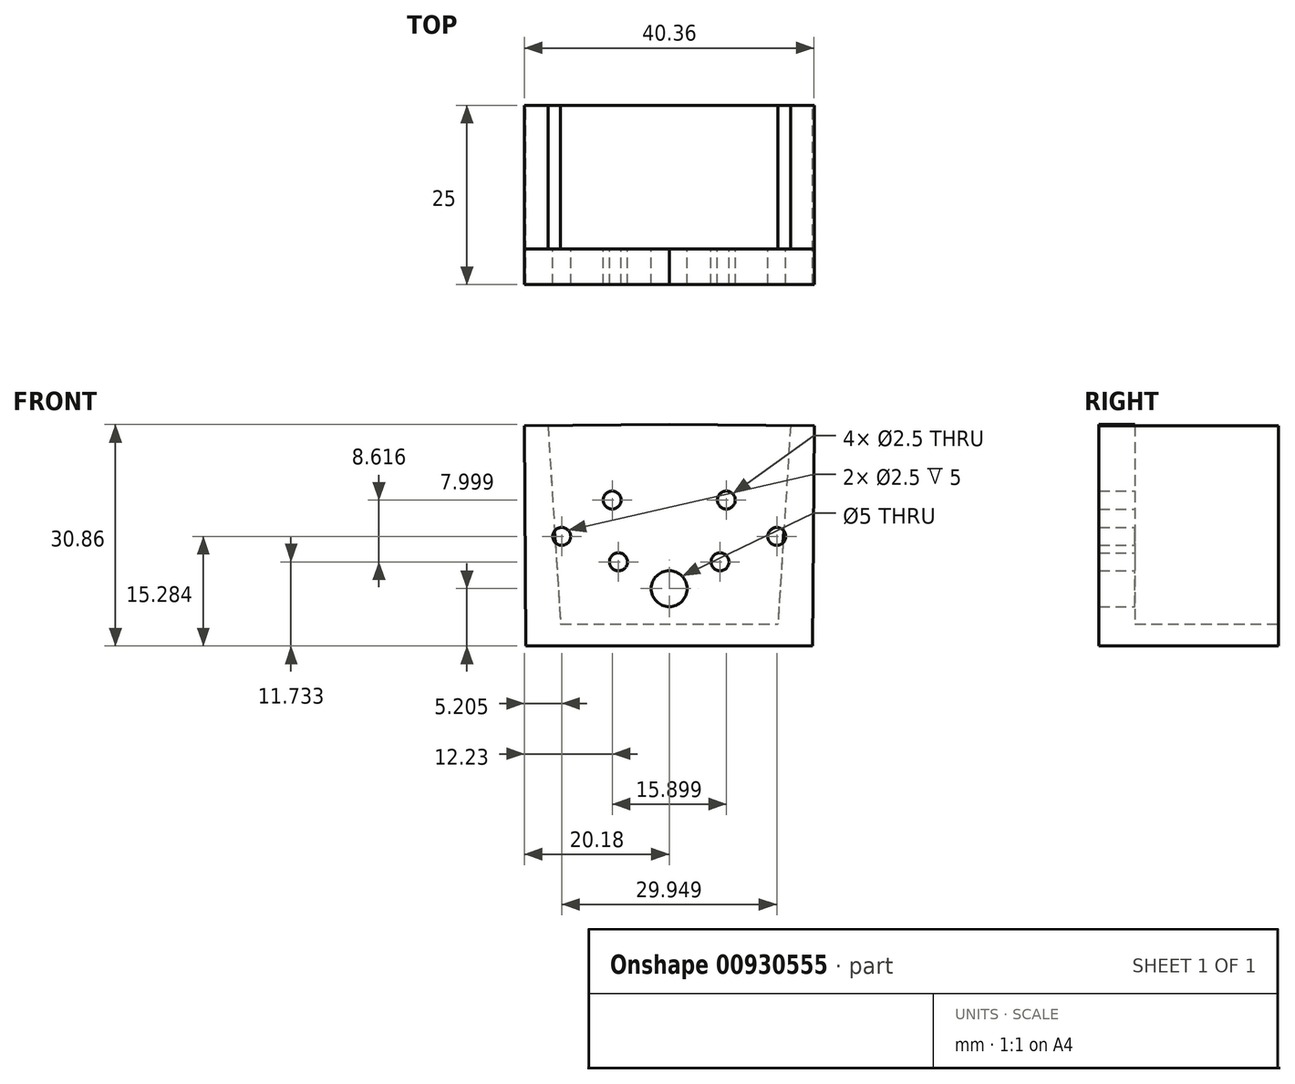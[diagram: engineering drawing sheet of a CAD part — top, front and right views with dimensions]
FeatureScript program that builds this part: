
annotation { "Feature Type Name" : "Feature", "Feature Type Description" : "" }
export const myFeature = defineFeature(function(context is Context, id is Id, definition is map)
    precondition{}
    {
        {
            var Q0;
            Q0=qCreatedBy(makeId("Front.planeOp"),FACE);
            var sketch = newSketch(context, id + "F0", { "sketchPlane" : qUnion([Q0])});
            skLineSegment(sketch, "E0", {"start": v(0, 0) * mm, "end": v(-19.97, 0) * mm});
            skLineSegment(sketch, "E1", {"start": v(-19.97, 0) * mm, "end": v(-20.18, 30.72) * mm});
            skLineSegment(sketch, "E2", {"start": v(-20.18, 30.72) * mm, "end": v(-16.9, 30.72) * mm});
            skLineSegment(sketch, "E3", {"start": v(-16.9, 30.72) * mm, "end": v(-15.14, 3.07) * mm});
            skLineSegment(sketch, "E4", {"start": v(-15.14, 3.07) * mm, "end": v(0, 3.07) * mm});
            skLineSegment(sketch, "E5", {"start": v(0, 3.07) * mm, "end": v(0, 0) * mm});
            skLineSegment(sketch, "E6", {"start": v(0, 39.93) * mm, "end": v(0, -20.84) * mm, "construction": true});
            skSolve(sketch);
        }
        {
            var Q0;
            Q0=makeQuery(id+"F0.imprint","IMPRINT",FACE,{"disambiguationData":[TD([[makeQuery(id+"F0.imprint","IMPRINT",EDGE,{"derivedFrom":sQuery(id+"F0.wireOp",EDGE,"E0")}),-1.0]])]});
            extrude(context, id + "F1", {"entities" : qUnion([Q0]), "depth" : 20 * mm, "offsetDistance" : 25 * mm});
        }
        {
            var Q0;
            Q0=makeQuery(id+"F1.opExtrude","CAP_FACE",FACE,{"disambiguationData":[OSD([sQuery(id+"F0.wireOp",EDGE,"E0"),sQuery(id+"F0.wireOp",EDGE,"E1"),sQuery(id+"F0.wireOp",EDGE,"E2"),sQuery(id+"F0.wireOp",EDGE,"E3"),sQuery(id+"F0.wireOp",EDGE,"E4"),sQuery(id+"F0.wireOp",EDGE,"E5")])],"isStart":false});
            var sketch = newSketch(context, id + "F2", { "sketchPlane" : qUnion([Q0])});
            skLineSegment(sketch, "E7", {"start": v(-20.18, 30.72) * mm, "end": v(0, 30.86) * mm});
            skLineSegment(sketch, "E8", {"start": v(0, 30.86) * mm, "end": v(0, 0) * mm});
            skLineSegment(sketch, "E9", {"start": v(0, 0) * mm, "end": v(-19.97, 0) * mm});
            skLineSegment(sketch, "E10", {"start": v(-19.97, 0) * mm, "end": v(-20.18, 30.72) * mm});
            skCircle(sketch, "E11", {"center": v(-10, 15.79) * mm, "radius": 5 * mm, "construction": true});
            skPoint(sketch, "E12", {"position": v(-14.97, 15.28) * mm});
            skPoint(sketch, "E13.1.0", {"position": v(-7.08, 11.73) * mm});
            skPoint(sketch, "E13.2.0", {"position": v(-7.95, 20.35) * mm});
            skCircle(sketch, "E14", {"center": v(0, 8) * mm, "radius": 2.39 * mm});
            skCircle(sketch, "E15", {"center": v(0, 8) * mm, "radius": 2.5 * mm});
            skSolve(sketch);
        }
        {
            var Q0;
            {var subQ2=sQuery(id+"F2.wireOp",EDGE,"E7");Q0=makeQuery(id+"F2.imprint","IMPRINT",FACE,{"disambiguationData":[TD([[makeQuery(id+"F2.imprint","IMPRINT",EDGE,{"derivedFrom":subQ2}),-1.0]])]});}
            var Q1;
            {var subQ0=sQuery(id+"F2.wireOp",EDGE,"E9");Q1=makeQuery(id+"F2.imprint","IMPRINT",FACE,{"disambiguationData":[TD([[makeQuery(id+"F2.imprint","IMPRINT",EDGE,{"derivedFrom":subQ0}),-1.0]])]});}
            extrude(context, id + "F3", {"entities" : qUnion([Q0, Q1]), "operationType" : NewBodyOperationType.ADD, "depth" : 5 * mm, "offsetDistance" : 25 * mm});
        }
        {
            var Q0;
            Q0=sQuery(id+"F2.wireOp",VERTEX,"E12");
            var Q1;
            Q1=sQuery(id+"F2.wireOp",VERTEX,"E13.1.0");
            var Q2;
            Q2=sQuery(id+"F2.wireOp",VERTEX,"E13.2.0");
            var Q3;
            Q3=makeQuery(id+"F1.opExtrude","SWEPT_BODY",BODY,{"disambiguationData":[OSD([sQuery(id+"F0.wireOp",EDGE,"E0"),sQuery(id+"F0.wireOp",EDGE,"E1"),sQuery(id+"F0.wireOp",EDGE,"E2"),sQuery(id+"F0.wireOp",EDGE,"E3"),sQuery(id+"F0.wireOp",EDGE,"E4"),sQuery(id+"F0.wireOp",EDGE,"E5")])]});
            hole(context, id + "F4", {"style" : HoleStyle.SIMPLE, "endStyle" : HoleEndStyle.THROUGH, "oppositeDirection" : true, "standardTappedOrClearance" : lookupTablePath({ "standard" : "ISO", "size" : "2.5", "type" : "Drilled" }), "standardBlindInLast" : lookupTablePath({ "standard" : "ISO", "size" : "2.5", "type" : "Drilled" }), "holeDiameter" : 2.5 * mm, "majorDiameter" : 5 * mm, "isTappedThrough" : true, "tappedDepth" : 12 * mm, "tapClearance" : 3, "startFromSketch" : true, "locations" : qUnion([Q0, Q1, Q2]), "scope" : qUnion([Q3])});
        }
        {
            var Q0;
            Q0=makeQuery(id+"F1.opExtrude","SWEPT_BODY",BODY,{"disambiguationData":[OSD([sQuery(id+"F0.wireOp",EDGE,"E0"),sQuery(id+"F0.wireOp",EDGE,"E1"),sQuery(id+"F0.wireOp",EDGE,"E2"),sQuery(id+"F0.wireOp",EDGE,"E3"),sQuery(id+"F0.wireOp",EDGE,"E4"),sQuery(id+"F0.wireOp",EDGE,"E5")])]});
            var Q1;
            Q1=qCreatedBy(makeId("Right.planeOp"),FACE);
            mirror(context, id + "F5", {"operationType" : NewBodyOperationType.ADD, "entities" : qUnion([Q0]), "mirrorPlane" : qUnion([Q1])});
        }
    });
